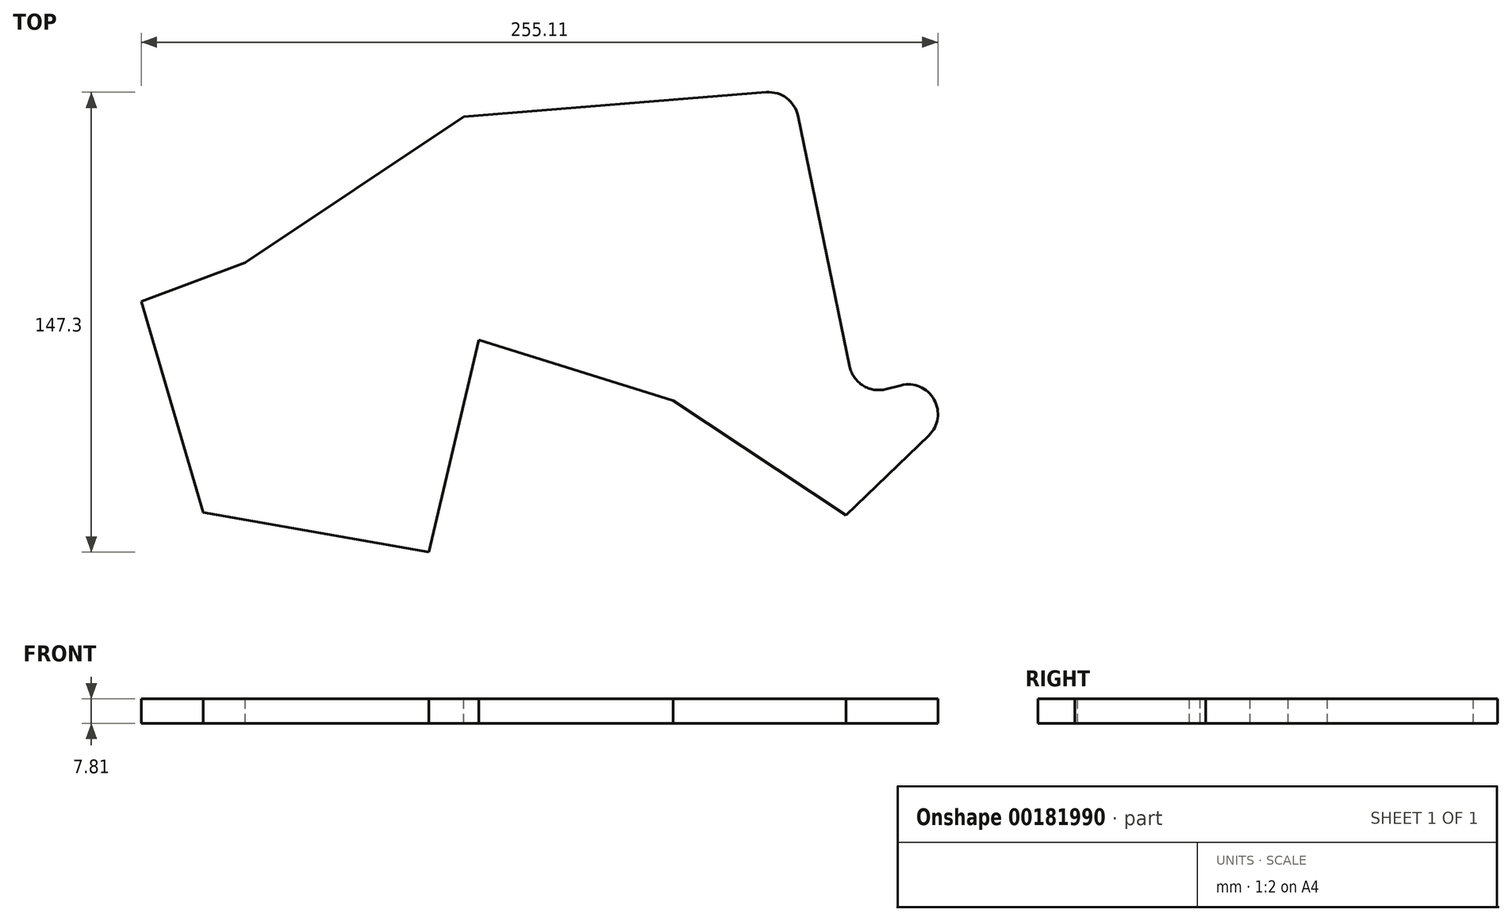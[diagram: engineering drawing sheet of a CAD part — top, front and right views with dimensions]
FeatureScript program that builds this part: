
annotation { "Feature Type Name" : "Feature", "Feature Type Description" : "" }
export const myFeature = defineFeature(function(context is Context, id is Id, definition is map)
    precondition{}
    {
        {
            var Q0;
            Q0=qCreatedBy(makeId("Top.planeOp"),FACE);
            var sketch = newSketch(context, id + "F0", { "sketchPlane" : qUnion([Q0])});
            skLineSegment(sketch, "E0", {"start": v(52.64, -54.87) * mm, "end": v(32.36, 43.37) * mm});
            skLineSegment(sketch, "E1", {"start": v(32.36, 43.37) * mm, "end": v(-72.95, 34.94) * mm});
            skLineSegment(sketch, "E2", {"start": v(-72.95, 34.94) * mm, "end": v(-142.93, -11.79) * mm});
            skLineSegment(sketch, "E3", {"start": v(-142.93, -11.79) * mm, "end": v(-176.2, -24.32) * mm});
            skLineSegment(sketch, "E4", {"start": v(-176.2, -24.32) * mm, "end": v(-156.38, -91.8) * mm});
            skLineSegment(sketch, "E5", {"start": v(-156.38, -91.8) * mm, "end": v(-84.12, -104.56) * mm});
            skLineSegment(sketch, "E6", {"start": v(-84.12, -104.56) * mm, "end": v(-68.16, -36.63) * mm});
            skLineSegment(sketch, "E7", {"start": v(-68.16, -36.63) * mm, "end": v(-5.94, -56) * mm});
            skLineSegment(sketch, "E8", {"start": v(-5.94, -56) * mm, "end": v(49.45, -92.7) * mm});
            skLineSegment(sketch, "E9", {"start": v(49.45, -92.7) * mm, "end": v(102.1, -42.1) * mm});
            skLineSegment(sketch, "E10", {"start": v(102.1, -42.1) * mm, "end": v(52.64, -54.87) * mm});
            skSolve(sketch);
        }
        {
            var Q0;
            Q0=makeQuery(id+"F0.imprint","IMPRINT",FACE,{"disambiguationData":[TD([[makeQuery(id+"F0.imprint","IMPRINT",EDGE,{"derivedFrom":sQuery(id+"F0.wireOp",EDGE,"E0")}),1.0]])]});
            extrude(context, id + "F1", {"entities" : qUnion([Q0]), "oppositeDirection" : true, "depth" : 7.8 * mm});
        }
        {
            var Q0;
            Q0=makeQuery(id+"F1.opExtrude","SWEPT_EDGE",EDGE,{"disambiguationData":[OSD([sQuery(id+"F0.wireOp",EDGE,"E9"),sQuery(id+"F0.wireOp",EDGE,"E10")])]});
            var Q1;
            Q1=makeQuery(id+"F1.opExtrude","SWEPT_EDGE",EDGE,{"disambiguationData":[OSD([sQuery(id+"F0.wireOp",EDGE,"E0"),sQuery(id+"F0.wireOp",EDGE,"E10")])]});
            var Q2;
            Q2=makeQuery(id+"F1.opExtrude","SWEPT_EDGE",EDGE,{"disambiguationData":[OSD([sQuery(id+"F0.wireOp",EDGE,"E0"),sQuery(id+"F0.wireOp",EDGE,"E1")])]});
            fillet(context, id + "F2", {"entities" : qUnion([Q0, Q1, Q2]), "radius" : 9.5 * mm, "tangentPropagation" : true, "allowEdgeOverflow" : false});
        }
    });
